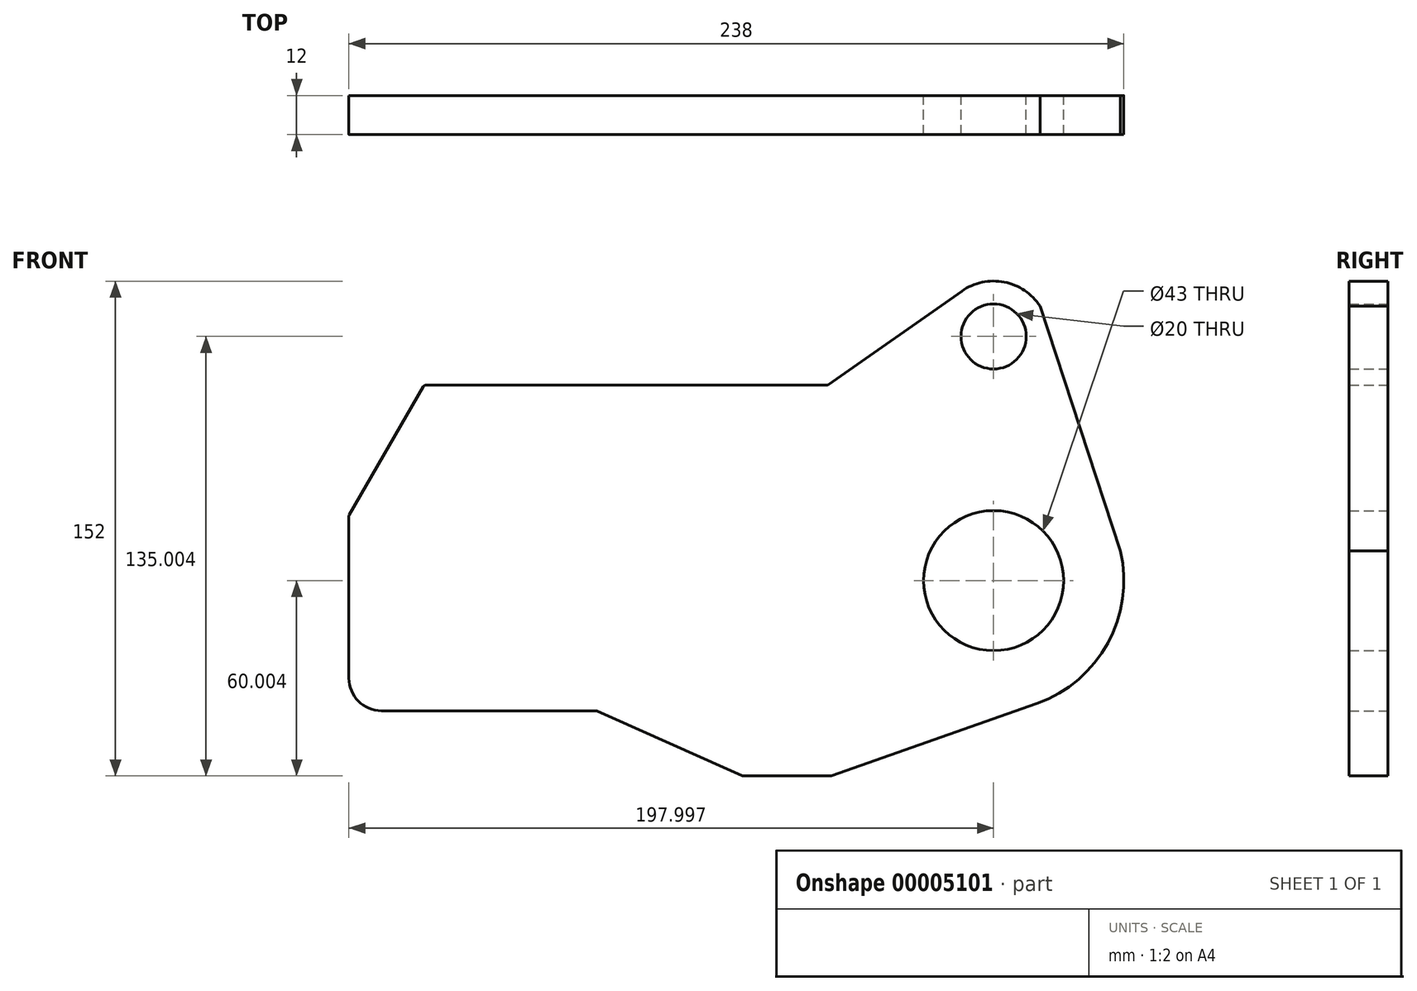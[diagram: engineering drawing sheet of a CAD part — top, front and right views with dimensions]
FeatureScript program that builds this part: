
annotation { "Feature Type Name" : "Feature", "Feature Type Description" : "" }
export const myFeature = defineFeature(function(context is Context, id is Id, definition is map)
    precondition{}
    {
        {
            var Q0;
            Q0=qCreatedBy(makeId("Front.planeOp"),FACE);
            var sketch = newSketch(context, id + "F0", { "sketchPlane" : qUnion([Q0])});
            skCircle(sketch, "E0", {"center": v(53.45, 4.91) * mm, "radius": 21.5 * mm});
            skCircle(sketch, "E1", {"center": v(53.45, 79.91) * mm, "radius": 10 * mm});
            skArc(sketch, "E2", {"start": v(67.7, 89.17) * mm, "mid": v(56.7, 96.6) * mm, "end": v(43.7, 93.84) * mm});
            skArc(sketch, "E3", {"start": v(66.72, -32.82) * mm, "mid": v(88.52, -14.32) * mm, "end": v(92.4, 14) * mm});
            skLineSegment(sketch, "E4", {"start": v(2.45, 64.96) * mm, "end": v(-121.43, 64.96) * mm});
            skLineSegment(sketch, "E5", {"start": v(-121.43, 64.96) * mm, "end": v(-144.55, 24.91) * mm});
            skLineSegment(sketch, "E6", {"start": v(-144.55, 24.91) * mm, "end": v(-144.55, -25.04) * mm});
            skLineSegment(sketch, "E7", {"start": v(-134.55, -35.04) * mm, "end": v(-68.55, -35.04) * mm});
            skLineSegment(sketch, "E8", {"start": v(-68.55, -35.04) * mm, "end": v(-23.55, -55.09) * mm});
            skLineSegment(sketch, "E9", {"start": v(-23.55, -55.09) * mm, "end": v(3.45, -55.09) * mm});
            skLineSegment(sketch, "E10", {"start": v(3.45, -55.09) * mm, "end": v(66.72, -32.82) * mm});
            skPoint(sketch, "E11.visualSharp", {"position": v(-144.55, -35.04) * mm});
            skArc(sketch, "E11.filletArc", {"start": v(-144.55, -25.04) * mm, "mid": v(-141.62, -32.11) * mm, "end": v(-134.55, -35.04) * mm});
            skLineSegment(sketch, "E12", {"start": v(2.45, 64.96) * mm, "end": v(43.7, 93.84) * mm});
            skLineSegment(sketch, "E13", {"start": v(67.7, 89.17) * mm, "end": v(92.4, 14) * mm});
            skSolve(sketch);
        }
        {
            var Q0;
            Q0=makeQuery(id+"F0.imprint","IMPRINT",FACE,{"disambiguationData":[TD([[makeQuery(id+"F0.imprint","IMPRINT",EDGE,{"derivedFrom":sQuery(id+"F0.wireOp",EDGE,"E0")}),-1.0]])]});
            extrude(context, id + "F1", {"entities" : qUnion([Q0]), "depth" : 12 * mm});
        }
        {
            var Q0;
            Q0=makeQuery(id+"F1.opExtrude","SWEPT_EDGE",EDGE,{"disambiguationData":[OSD([sQuery(id+"F0.wireOp",EDGE,"E4"),sQuery(id+"F0.wireOp",EDGE,"E5")])]});
            var Q1;
            Q1=makeQuery(id+"F1.opExtrude","SWEPT_EDGE",EDGE,{"disambiguationData":[OSD([sQuery(id+"F0.wireOp",EDGE,"E5"),sQuery(id+"F0.wireOp",EDGE,"E6")])]});
            var Q2;
            Q2=makeQuery(id+"F1.opExtrude","SWEPT_EDGE",EDGE,{"disambiguationData":[OSD([sQuery(id+"F0.wireOp",EDGE,"E4"),sQuery(id+"F0.wireOp",EDGE,"E12")])]});
            var Q3;
            Q3=makeQuery(id+"F1.opExtrude","SWEPT_EDGE",EDGE,{"disambiguationData":[OSD([sQuery(id+"F0.wireOp",EDGE,"E8"),sQuery(id+"F0.wireOp",EDGE,"E9")])]});
            var Q4;
            Q4=makeQuery(id+"F1.opExtrude","SWEPT_EDGE",EDGE,{"disambiguationData":[OSD([sQuery(id+"F0.wireOp",EDGE,"E9"),sQuery(id+"F0.wireOp",EDGE,"E10")])]});
            var Q5;
            Q5=makeQuery(id+"F1.opExtrude","SWEPT_EDGE",EDGE,{"disambiguationData":[OSD([sQuery(id+"F0.wireOp",EDGE,"E7"),sQuery(id+"F0.wireOp",EDGE,"E8")])]});
            fillet(context, id + "F2", {"entities" : qUnion([Q0, Q1, Q2, Q3, Q4, Q5]), "radius" : 1 * mm, "tangentPropagation" : true, "allowEdgeOverflow" : false});
        }
    });
